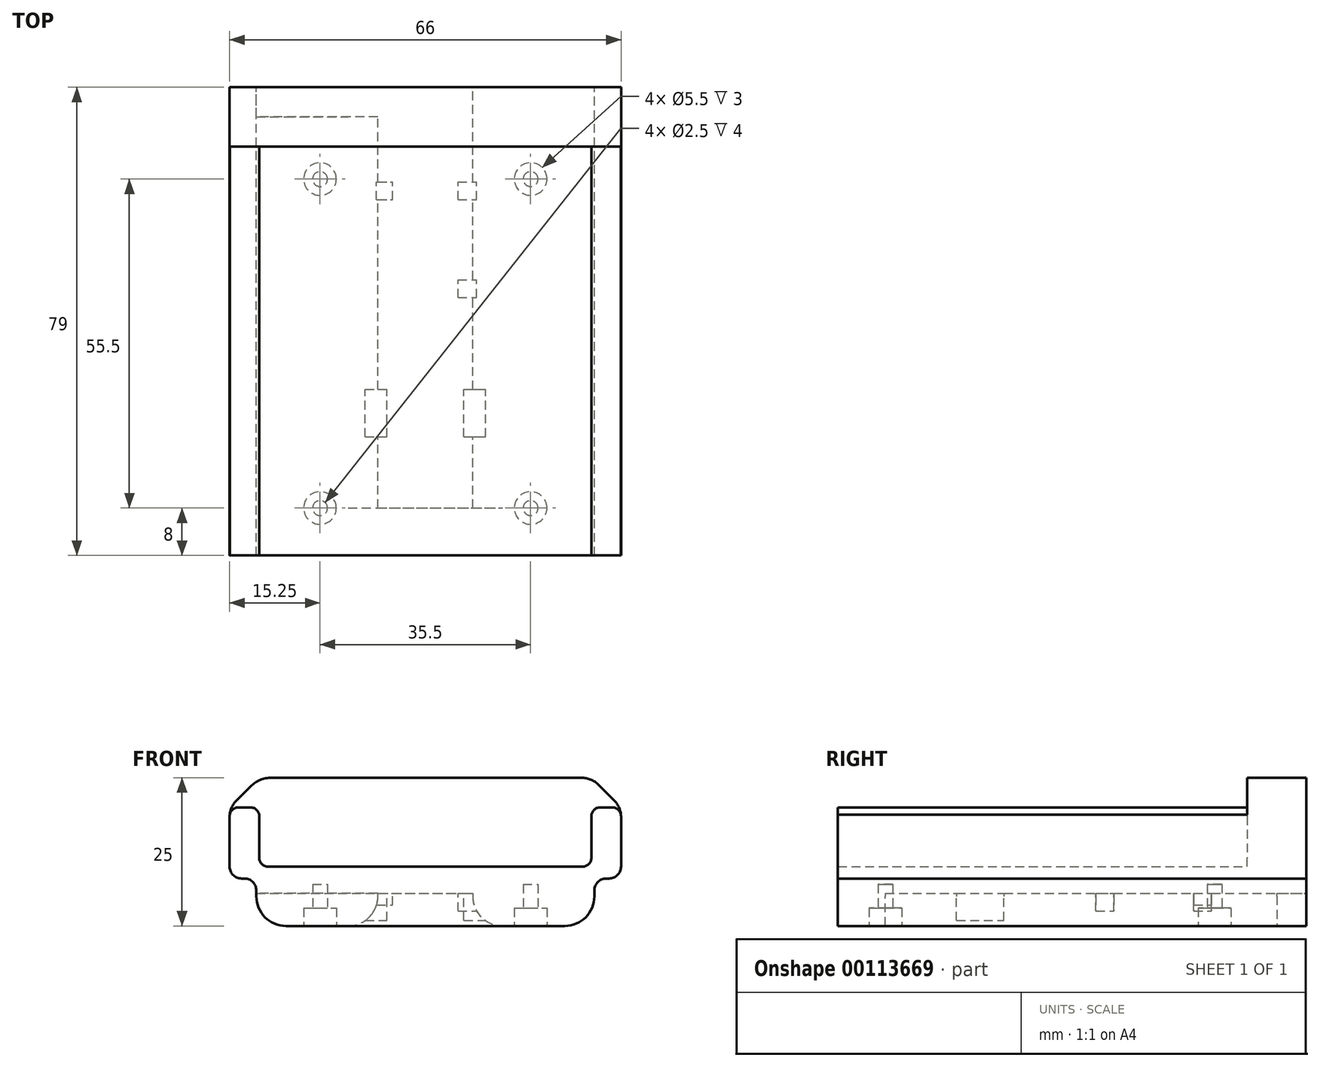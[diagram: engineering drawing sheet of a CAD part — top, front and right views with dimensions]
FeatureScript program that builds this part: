
annotation { "Feature Type Name" : "Feature", "Feature Type Description" : "" }
export const myFeature = defineFeature(function(context is Context, id is Id, definition is map)
    precondition{}
    {
        {
            var Q0;
            Q0=qCreatedBy(makeId("Front.planeOp"),FACE);
            var sketch = newSketch(context, id + "F0", { "sketchPlane" : qUnion([Q0])});
            skLineSegment(sketch, "E0.bottom", {"start": v(-33, 12.5) * mm, "end": v(33, 12.5) * mm});
            skLineSegment(sketch, "E0.top", {"start": v(-23.5, -12.5) * mm, "end": v(-13, -12.5) * mm});
            skLineSegment(sketch, "E0.left", {"start": v(-33, 12.5) * mm, "end": v(-33, -2.5) * mm});
            skLineSegment(sketch, "E0.right", {"start": v(33, 12.5) * mm, "end": v(33, -2.5) * mm});
            skLineSegment(sketch, "E1", {"start": v(28.5, -6.5) * mm, "end": v(28.5, -7.5) * mm});
            skLineSegment(sketch, "E2", {"start": v(-33, -4.5) * mm, "end": v(-33, -4.5) * mm});
            skLineSegment(sketch, "E3", {"start": v(-31, -4.5) * mm, "end": v(-30.5, -4.5) * mm});
            skLineSegment(sketch, "E4", {"start": v(-28.5, -6.5) * mm, "end": v(-28.5, -7.5) * mm});
            skArc(sketch, "E5.filletArc", {"start": v(-28.5, -6.5) * mm, "mid": v(-29.09, -5.09) * mm, "end": v(-30.5, -4.5) * mm});
            skLineSegment(sketch, "E6", {"start": v(30.5, -4.5) * mm, "end": v(31, -4.5) * mm});
            skPoint(sketch, "E7.visualSharp", {"position": v(28.5, -4.5) * mm});
            skArc(sketch, "E7.filletArc", {"start": v(30.5, -4.5) * mm, "mid": v(29.09, -5.09) * mm, "end": v(28.5, -6.5) * mm});
            skArc(sketch, "E8.filletArc", {"start": v(-33, -2.5) * mm, "mid": v(-32.41, -3.91) * mm, "end": v(-31, -4.5) * mm});
            skPoint(sketch, "E9.visualSharp", {"position": v(33, -4.5) * mm});
            skArc(sketch, "E9.filletArc", {"start": v(31, -4.5) * mm, "mid": v(32.41, -3.91) * mm, "end": v(33, -2.5) * mm});
            skLineSegment(sketch, "E10.bottom", {"start": v(-8, -7) * mm, "end": v(8, -7) * mm});
            skLineSegment(sketch, "E10.left", {"start": v(-8, -7) * mm, "end": v(-8, -7.5) * mm});
            skLineSegment(sketch, "E10.right", {"start": v(8, -7) * mm, "end": v(8, -7.5) * mm});
            skLineSegment(sketch, "E11.trimOffspring", {"start": v(13, -12.5) * mm, "end": v(23.5, -12.5) * mm});
            skPoint(sketch, "E12.visualSharp", {"position": v(-28.5, -12.5) * mm});
            skArc(sketch, "E12.filletArc", {"start": v(-28.5, -7.5) * mm, "mid": v(-27.04, -11.04) * mm, "end": v(-23.5, -12.5) * mm});
            skPoint(sketch, "E13.visualSharp", {"position": v(-8, -12.5) * mm});
            skArc(sketch, "E13.filletArc", {"start": v(-13, -12.5) * mm, "mid": v(-9.46, -11.04) * mm, "end": v(-8, -7.5) * mm});
            skPoint(sketch, "E14.visualSharp", {"position": v(8, -12.5) * mm});
            skArc(sketch, "E14.filletArc", {"start": v(8, -7.5) * mm, "mid": v(9.46, -11.04) * mm, "end": v(13, -12.5) * mm});
            skPoint(sketch, "E15.visualSharp", {"position": v(28.5, -12.5) * mm});
            skArc(sketch, "E15.filletArc", {"start": v(23.5, -12.5) * mm, "mid": v(27.04, -11.04) * mm, "end": v(28.5, -7.5) * mm});
            skSolve(sketch);
        }
        {
            var Q0;
            Q0 = qSketchRegion(id + "F0", true);
            extrude(context, id + "F1", {"entities" : qUnion([Q0]), "depth" : 71 * mm});
        }
        {
            var Q0;
            Q0=makeQuery(id+"F1.opExtrude","CAP_FACE",FACE,{"disambiguationData":[OSD([sQuery(id+"F0.wireOp",EDGE,"E0.bottom"),sQuery(id+"F0.wireOp",EDGE,"E0.top"),sQuery(id+"F0.wireOp",EDGE,"E0.left"),sQuery(id+"F0.wireOp",EDGE,"E0.right"),sQuery(id+"F0.wireOp",EDGE,"E1"),sQuery(id+"F0.wireOp",EDGE,"E3"),sQuery(id+"F0.wireOp",EDGE,"E4"),sQuery(id+"F0.wireOp",EDGE,"E5.filletArc"),sQuery(id+"F0.wireOp",EDGE,"E6"),sQuery(id+"F0.wireOp",EDGE,"E7.filletArc"),sQuery(id+"F0.wireOp",EDGE,"E8.filletArc"),sQuery(id+"F0.wireOp",EDGE,"E9.filletArc"),sQuery(id+"F0.wireOp",EDGE,"E10.bottom"),sQuery(id+"F0.wireOp",EDGE,"E10.left"),sQuery(id+"F0.wireOp",EDGE,"E10.right"),sQuery(id+"F0.wireOp",EDGE,"E11.trimOffspring"),sQuery(id+"F0.wireOp",EDGE,"E12.filletArc"),sQuery(id+"F0.wireOp",EDGE,"E13.filletArc"),sQuery(id+"F0.wireOp",EDGE,"E14.filletArc"),sQuery(id+"F0.wireOp",EDGE,"E15.filletArc")])],"isStart":false});
            var sketch = newSketch(context, id + "F2", { "sketchPlane" : qUnion([Q0])});
            skLineSegment(sketch, "E16", {"start": v(33, 6) * mm, "end": v(33, -2.32) * mm});
            skLineSegment(sketch, "E17", {"start": v(-23.5, -12.5) * mm, "end": v(23.5, -12.5) * mm});
            skLineSegment(sketch, "E18", {"start": v(-28.5, -6.5) * mm, "end": v(-28.5, -7.5) * mm});
            skLineSegment(sketch, "E19", {"start": v(28.5, -6.5) * mm, "end": v(28.5, -7.5) * mm});
            skPoint(sketch, "E20.trimOffspring.start.orphan", {"position": v(-33, -12.5) * mm});
            skPoint(sketch, "E21.orphan", {"position": v(-33, -7) * mm});
            skLineSegment(sketch, "E22", {"start": v(-33, 6) * mm, "end": v(-33, -2.5) * mm});
            skLineSegment(sketch, "E23", {"start": v(-33, -2.5) * mm, "end": v(-33, -2.5) * mm});
            skLineSegment(sketch, "E24", {"start": v(-31, -4.5) * mm, "end": v(-30.5, -4.5) * mm});
            skLineSegment(sketch, "E25", {"start": v(33, -2.32) * mm, "end": v(33, -2.5) * mm});
            skLineSegment(sketch, "E26", {"start": v(31, -4.5) * mm, "end": v(30.5, -4.5) * mm});
            skPoint(sketch, "E27.visualSharp", {"position": v(33, -4.5) * mm});
            skArc(sketch, "E27.filletArc", {"start": v(31, -4.5) * mm, "mid": v(32.41, -3.91) * mm, "end": v(33, -2.5) * mm});
            skPoint(sketch, "E28.newPointB", {"position": v(28.5, -2.32) * mm});
            skArc(sketch, "E28.filletArc", {"start": v(30.5, -4.5) * mm, "mid": v(29.09, -5.09) * mm, "end": v(28.5, -6.5) * mm});
            skPoint(sketch, "E29.visualSharp", {"position": v(-33, -4.5) * mm});
            skArc(sketch, "E29.filletArc", {"start": v(-33, -2.5) * mm, "mid": v(-32.41, -3.91) * mm, "end": v(-31, -4.5) * mm});
            skPoint(sketch, "E30.newPointB", {"position": v(-28.5, -2.49) * mm});
            skArc(sketch, "E30.filletArc", {"start": v(-28.5, -6.5) * mm, "mid": v(-29.09, -5.09) * mm, "end": v(-30.5, -4.5) * mm});
            skPoint(sketch, "E31.visualSharp", {"position": v(-28.5, -12.5) * mm});
            skArc(sketch, "E31.filletArc", {"start": v(-28.5, -7.5) * mm, "mid": v(-27.04, -11.04) * mm, "end": v(-23.5, -12.5) * mm});
            skPoint(sketch, "E32.visualSharp", {"position": v(28.5, -12.5) * mm});
            skArc(sketch, "E32.filletArc", {"start": v(23.5, -12.5) * mm, "mid": v(27.04, -11.04) * mm, "end": v(28.5, -7.5) * mm});
            skLineSegment(sketch, "E33", {"start": v(-31.5, 7.5) * mm, "end": v(-29.5, 7.5) * mm});
            skLineSegment(sketch, "E34", {"start": v(-28, 6) * mm, "end": v(-28, -1) * mm});
            skLineSegment(sketch, "E35", {"start": v(28, 6) * mm, "end": v(28, -1) * mm});
            skLineSegment(sketch, "E36", {"start": v(-26.5, -2.5) * mm, "end": v(26.5, -2.5) * mm});
            skLineSegment(sketch, "E37.trimOffspring", {"start": v(29.5, 7.5) * mm, "end": v(31.5, 7.5) * mm});
            skPoint(sketch, "E38.visualSharp", {"position": v(-33, 7.5) * mm});
            skArc(sketch, "E38.filletArc", {"start": v(-31.5, 7.5) * mm, "mid": v(-32.56, 7.06) * mm, "end": v(-33, 6) * mm});
            skPoint(sketch, "E39.visualSharp", {"position": v(-28, 7.5) * mm});
            skArc(sketch, "E39.filletArc", {"start": v(-28, 6) * mm, "mid": v(-28.44, 7.06) * mm, "end": v(-29.5, 7.5) * mm});
            skPoint(sketch, "E40.visualSharp", {"position": v(33, 7.5) * mm});
            skArc(sketch, "E40.filletArc", {"start": v(33, 6) * mm, "mid": v(32.56, 7.06) * mm, "end": v(31.5, 7.5) * mm});
            skPoint(sketch, "E41.visualSharp", {"position": v(28, 7.5) * mm});
            skArc(sketch, "E41.filletArc", {"start": v(29.5, 7.5) * mm, "mid": v(28.44, 7.06) * mm, "end": v(28, 6) * mm});
            skPoint(sketch, "E42.visualSharp", {"position": v(-28, -2.5) * mm});
            skArc(sketch, "E42.filletArc", {"start": v(-28, -1) * mm, "mid": v(-27.56, -2.06) * mm, "end": v(-26.5, -2.5) * mm});
            skPoint(sketch, "E43.visualSharp", {"position": v(28, -2.5) * mm});
            skArc(sketch, "E43.filletArc", {"start": v(26.5, -2.5) * mm, "mid": v(27.56, -2.06) * mm, "end": v(28, -1) * mm});
            skSolve(sketch);
        }
        {
            var Q0;
            Q0 = qSketchRegion(id + "F2", true);
            extrude(context, id + "F3", {"entities" : qUnion([Q0]), "operationType" : NewBodyOperationType.ADD, "depth" : 8 * mm});
        }
        {
            var Q0;
            Q0=makeQuery(id+"F1.opExtrude","CAP_FACE",FACE,{"disambiguationData":[OSD([sQuery(id+"F0.wireOp",EDGE,"E0.bottom"),sQuery(id+"F0.wireOp",EDGE,"E0.top"),sQuery(id+"F0.wireOp",EDGE,"E0.left"),sQuery(id+"F0.wireOp",EDGE,"E0.right"),sQuery(id+"F0.wireOp",EDGE,"E1"),sQuery(id+"F0.wireOp",EDGE,"E3"),sQuery(id+"F0.wireOp",EDGE,"E4"),sQuery(id+"F0.wireOp",EDGE,"E5.filletArc"),sQuery(id+"F0.wireOp",EDGE,"E6"),sQuery(id+"F0.wireOp",EDGE,"E7.filletArc"),sQuery(id+"F0.wireOp",EDGE,"E8.filletArc"),sQuery(id+"F0.wireOp",EDGE,"E9.filletArc"),sQuery(id+"F0.wireOp",EDGE,"E10.bottom"),sQuery(id+"F0.wireOp",EDGE,"E10.left"),sQuery(id+"F0.wireOp",EDGE,"E10.right"),sQuery(id+"F0.wireOp",EDGE,"E11.trimOffspring"),sQuery(id+"F0.wireOp",EDGE,"E12.filletArc"),sQuery(id+"F0.wireOp",EDGE,"E13.filletArc"),sQuery(id+"F0.wireOp",EDGE,"E14.filletArc"),sQuery(id+"F0.wireOp",EDGE,"E15.filletArc")])],"isStart":false});
            var sketch = newSketch(context, id + "F4", { "sketchPlane" : qUnion([Q0])});
            skLineSegment(sketch, "E44", {"start": v(-33, 6) * mm, "end": v(-33, 6) * mm});
            skLineSegment(sketch, "E45", {"start": v(-28, 6) * mm, "end": v(-28, -1) * mm});
            skLineSegment(sketch, "E46", {"start": v(-26.5, -2.5) * mm, "end": v(26.5, -2.5) * mm});
            skLineSegment(sketch, "E47", {"start": v(28, -1) * mm, "end": v(28, 6) * mm});
            skLineSegment(sketch, "E48", {"start": v(29.5, 7.5) * mm, "end": v(31.5, 7.5) * mm});
            skLineSegment(sketch, "E49", {"start": v(33, 12.5) * mm, "end": v(-33, 12.5) * mm});
            skLineSegment(sketch, "E50", {"start": v(-31.5, 7.5) * mm, "end": v(-29.5, 7.5) * mm});
            skLineSegment(sketch, "E51", {"start": v(-28, 6) * mm, "end": v(-28, 6) * mm});
            skPoint(sketch, "E52.newPointA", {"position": v(-33, 7.5) * mm});
            skArc(sketch, "E52.filletArc", {"start": v(-31.5, 7.5) * mm, "mid": v(-32.56, 7.06) * mm, "end": v(-33, 6) * mm});
            skPoint(sketch, "E53.visualSharp", {"position": v(-28, 7.5) * mm});
            skArc(sketch, "E53.filletArc", {"start": v(-28, 6) * mm, "mid": v(-28.44, 7.06) * mm, "end": v(-29.5, 7.5) * mm});
            skLineSegment(sketch, "E54", {"start": v(-33, 12.5) * mm, "end": v(-33, 6) * mm});
            skPoint(sketch, "E55.visualSharp", {"position": v(-28, -2.5) * mm});
            skArc(sketch, "E55.filletArc", {"start": v(-28, -1) * mm, "mid": v(-27.56, -2.06) * mm, "end": v(-26.5, -2.5) * mm});
            skPoint(sketch, "E56.visualSharp", {"position": v(28, -2.5) * mm});
            skArc(sketch, "E56.filletArc", {"start": v(26.5, -2.5) * mm, "mid": v(27.56, -2.06) * mm, "end": v(28, -1) * mm});
            skPoint(sketch, "E57.visualSharp", {"position": v(28, 7.5) * mm});
            skArc(sketch, "E57.filletArc", {"start": v(29.5, 7.5) * mm, "mid": v(28.44, 7.06) * mm, "end": v(28, 6) * mm});
            skArc(sketch, "E58.filletArc", {"start": v(33, 6) * mm, "mid": v(32.56, 7.06) * mm, "end": v(31.5, 7.5) * mm});
            skLineSegment(sketch, "E59", {"start": v(33, 6) * mm, "end": v(33, 12.5) * mm});
            skSolve(sketch);
        }
        {
            var Q0;
            Q0 = qSketchRegion(id + "F4", true);
            extrude(context, id + "F5", {"entities" : qUnion([Q0]), "operationType" : NewBodyOperationType.REMOVE, "oppositeDirection" : true, "depth" : 61 * mm});
        }
        {
            var Q0;
            Q0=makeQuery(id+"F1.opExtrude","SWEPT_EDGE",EDGE,{"disambiguationData":[OSD([sQuery(id+"F0.wireOp",EDGE,"E0.bottom"),sQuery(id+"F0.wireOp",EDGE,"E0.left")])]});
            chamfer(context, id + "F6", {"entities" : qUnion([Q0]), "width" : 5 * mm, "tangentPropagation" : true});
        }
        {
            var Q0;
            Q0=makeQuery(id+"F1.opExtrude","SWEPT_EDGE",EDGE,{"disambiguationData":[OSD([sQuery(id+"F0.wireOp",EDGE,"E0.bottom"),sQuery(id+"F0.wireOp",EDGE,"E0.right")])]});
            chamfer(context, id + "F7", {"entities" : qUnion([Q0]), "width" : 5 * mm, "tangentPropagation" : true});
        }
        {
            var Q0;
            {var subQ0=sQuery(id+"F0.wireOp",EDGE,"E0.bottom");Q0=makeQuery(id+"F7.opChamfer","BLEND_EDGE",EDGE,{"blendedFrom":[makeQuery(id+"F1.opExtrude","SWEPT_EDGE",EDGE,{"disambiguationData":[OSD([subQ0,sQuery(id+"F0.wireOp",EDGE,"E0.right")])]}),makeQuery(id+"F1.opExtrude","SWEPT_FACE",FACE,{"disambiguationData":[OSD([subQ0])]})],"blendedInto":[makeQuery(id+"F1.opExtrude","SWEPT_FACE",FACE,{"disambiguationData":[OSD([subQ0])]})]});}
            fillet(context, id + "F8", {"entities" : qUnion([Q0]), "radius" : 4 * mm, "tangentPropagation" : true, "allowEdgeOverflow" : false});
        }
        {
            var Q0;
            {var subQ0=sQuery(id+"F0.wireOp",EDGE,"E0.right");Q0=makeQuery(id+"F7.opChamfer","BLEND_EDGE",EDGE,{"blendedFrom":[makeQuery(id+"F1.opExtrude","SWEPT_EDGE",EDGE,{"disambiguationData":[OSD([sQuery(id+"F0.wireOp",EDGE,"E0.bottom"),subQ0])]}),makeQuery(id+"F3.boolean.opBoolean","MERGE",FACE,{"derivedFrom":[makeQuery(id+"F1.opExtrude","SWEPT_FACE",FACE,{"disambiguationData":[OSD([subQ0])]}),makeQuery(id+"F3.opExtrude","SWEPT_FACE",FACE,{"disambiguationData":[OSD([sQuery(id+"F2.wireOp",EDGE,"E16"),sQuery(id+"F2.wireOp",EDGE,"E25")])]})]})],"blendedInto":[makeQuery(id+"F3.boolean.opBoolean","MERGE",FACE,{"derivedFrom":[makeQuery(id+"F1.opExtrude","SWEPT_FACE",FACE,{"disambiguationData":[OSD([subQ0])]}),makeQuery(id+"F3.opExtrude","SWEPT_FACE",FACE,{"disambiguationData":[OSD([sQuery(id+"F2.wireOp",EDGE,"E16"),sQuery(id+"F2.wireOp",EDGE,"E25")])]})]})]});}
            fillet(context, id + "F9", {"entities" : qUnion([Q0]), "radius" : 4 * mm, "tangentPropagation" : true, "allowEdgeOverflow" : false});
        }
        {
            var Q0;
            {var subQ0=sQuery(id+"F0.wireOp",EDGE,"E0.left");Q0=makeQuery(id+"F6.opChamfer","BLEND_EDGE",EDGE,{"blendedFrom":[makeQuery(id+"F1.opExtrude","SWEPT_EDGE",EDGE,{"disambiguationData":[OSD([sQuery(id+"F0.wireOp",EDGE,"E0.bottom"),subQ0])]}),makeQuery(id+"F3.boolean.opBoolean","MERGE",FACE,{"derivedFrom":[makeQuery(id+"F1.opExtrude","SWEPT_FACE",FACE,{"disambiguationData":[OSD([subQ0])]}),makeQuery(id+"F3.opExtrude","SWEPT_FACE",FACE,{"disambiguationData":[OSD([sQuery(id+"F2.wireOp",EDGE,"E22")])]})]})],"blendedInto":[makeQuery(id+"F3.boolean.opBoolean","MERGE",FACE,{"derivedFrom":[makeQuery(id+"F1.opExtrude","SWEPT_FACE",FACE,{"disambiguationData":[OSD([subQ0])]}),makeQuery(id+"F3.opExtrude","SWEPT_FACE",FACE,{"disambiguationData":[OSD([sQuery(id+"F2.wireOp",EDGE,"E22")])]})]})]});}
            fillet(context, id + "F10", {"entities" : qUnion([Q0]), "radius" : 4 * mm, "tangentPropagation" : true, "allowEdgeOverflow" : false});
        }
        {
            var Q0;
            {var subQ0=sQuery(id+"F0.wireOp",EDGE,"E0.bottom");Q0=makeQuery(id+"F6.opChamfer","BLEND_EDGE",EDGE,{"blendedFrom":[makeQuery(id+"F1.opExtrude","SWEPT_EDGE",EDGE,{"disambiguationData":[OSD([subQ0,sQuery(id+"F0.wireOp",EDGE,"E0.left")])]}),makeQuery(id+"F1.opExtrude","SWEPT_FACE",FACE,{"disambiguationData":[OSD([subQ0])]})],"blendedInto":[makeQuery(id+"F1.opExtrude","SWEPT_FACE",FACE,{"disambiguationData":[OSD([subQ0])]})]});}
            fillet(context, id + "F11", {"entities" : qUnion([Q0]), "radius" : 5 * mm, "tangentPropagation" : true, "allowEdgeOverflow" : false});
        }
        {
            var Q0;
            Q0=makeQuery(id+"F1.opExtrude","SWEPT_FACE",FACE,{"disambiguationData":[OSD([sQuery(id+"F0.wireOp",EDGE,"E10.bottom")])]});
            var sketch = newSketch(context, id + "F12", { "sketchPlane" : qUnion([Q0])});
            skLineSegment(sketch, "E60.bottom", {"start": v(-11.5, 59) * mm, "end": v(-6.5, 59) * mm});
            skLineSegment(sketch, "E60.top", {"start": v(-11.5, 51) * mm, "end": v(-6.5, 51) * mm});
            skLineSegment(sketch, "E60.left", {"start": v(-11.5, 59) * mm, "end": v(-11.5, 51) * mm});
            skLineSegment(sketch, "E60.right", {"start": v(-6.5, 59) * mm, "end": v(-6.5, 51) * mm});
            skLineSegment(sketch, "E61.bottom", {"start": v(6.5, 59) * mm, "end": v(11.5, 59) * mm});
            skLineSegment(sketch, "E61.top", {"start": v(6.5, 51) * mm, "end": v(11.5, 51) * mm});
            skLineSegment(sketch, "E61.left", {"start": v(6.5, 59) * mm, "end": v(6.5, 51) * mm});
            skLineSegment(sketch, "E61.right", {"start": v(11.5, 59) * mm, "end": v(11.5, 51) * mm});
            skSolve(sketch);
        }
        {
            var Q0;
            Q0 = qSketchRegion(id + "F12", true);
            extrude(context, id + "F13", {"entities" : qUnion([Q0]), "operationType" : NewBodyOperationType.ADD, "depth" : 4.6 * mm});
        }
        {
            var Q0;
            Q0=makeQuery(id+"F1.opExtrude","SWEPT_FACE",FACE,{"disambiguationData":[OSD([sQuery(id+"F0.wireOp",EDGE,"E10.bottom")])]});
            var sketch = newSketch(context, id + "F14", { "sketchPlane" : qUnion([Q0])});
            skLineSegment(sketch, "E62.bottom", {"start": v(5.5, 35.5) * mm, "end": v(10.5, 35.5) * mm});
            skLineSegment(sketch, "E62.top", {"start": v(5.5, 32.5) * mm, "end": v(10.5, 32.5) * mm});
            skLineSegment(sketch, "E62.left", {"start": v(5.5, 35.5) * mm, "end": v(5.5, 32.5) * mm});
            skLineSegment(sketch, "E62.right", {"start": v(10.5, 35.5) * mm, "end": v(10.5, 32.5) * mm});
            skLineSegment(sketch, "E63.bottom", {"start": v(5.5, 19) * mm, "end": v(10.5, 19) * mm});
            skLineSegment(sketch, "E63.top", {"start": v(5.5, 16) * mm, "end": v(10.5, 16) * mm});
            skLineSegment(sketch, "E63.left", {"start": v(5.5, 19) * mm, "end": v(5.5, 16) * mm});
            skLineSegment(sketch, "E63.right", {"start": v(10.5, 19) * mm, "end": v(10.5, 16) * mm});
            skSolve(sketch);
        }
        {
            var Q0;
            Q0 = qSketchRegion(id + "F14", true);
            extrude(context, id + "F15", {"entities" : qUnion([Q0]), "operationType" : NewBodyOperationType.ADD, "depth" : 3 * mm});
        }
        {
            var Q0;
            Q0=makeQuery(id+"F1.opExtrude","SWEPT_FACE",FACE,{"disambiguationData":[OSD([sQuery(id+"F0.wireOp",EDGE,"E10.bottom")])]});
            var sketch = newSketch(context, id + "F16", { "sketchPlane" : qUnion([Q0])});
            skLineSegment(sketch, "E64.bottom", {"start": v(-10.5, 19) * mm, "end": v(-5.5, 19) * mm});
            skLineSegment(sketch, "E64.top", {"start": v(-10.5, 16) * mm, "end": v(-5.5, 16) * mm});
            skLineSegment(sketch, "E64.left", {"start": v(-10.5, 19) * mm, "end": v(-10.5, 16) * mm});
            skLineSegment(sketch, "E64.right", {"start": v(-5.5, 19) * mm, "end": v(-5.5, 16) * mm});
            skSolve(sketch);
        }
        {
            var Q0;
            Q0 = qSketchRegion(id + "F16", true);
            extrude(context, id + "F17", {"entities" : qUnion([Q0]), "operationType" : NewBodyOperationType.ADD, "depth" : 2 * mm});
        }
        {
            var Q0;
            Q0=makeQuery(id+"F1.opExtrude","CAP_FACE",FACE,{"disambiguationData":[OSD([sQuery(id+"F0.wireOp",EDGE,"E0.bottom"),sQuery(id+"F0.wireOp",EDGE,"E0.top"),sQuery(id+"F0.wireOp",EDGE,"E0.left"),sQuery(id+"F0.wireOp",EDGE,"E0.right"),sQuery(id+"F0.wireOp",EDGE,"E1"),sQuery(id+"F0.wireOp",EDGE,"E3"),sQuery(id+"F0.wireOp",EDGE,"E4"),sQuery(id+"F0.wireOp",EDGE,"E5.filletArc"),sQuery(id+"F0.wireOp",EDGE,"E6"),sQuery(id+"F0.wireOp",EDGE,"E7.filletArc"),sQuery(id+"F0.wireOp",EDGE,"E8.filletArc"),sQuery(id+"F0.wireOp",EDGE,"E9.filletArc"),sQuery(id+"F0.wireOp",EDGE,"E10.bottom"),sQuery(id+"F0.wireOp",EDGE,"E10.left"),sQuery(id+"F0.wireOp",EDGE,"E10.right"),sQuery(id+"F0.wireOp",EDGE,"E11.trimOffspring"),sQuery(id+"F0.wireOp",EDGE,"E12.filletArc"),sQuery(id+"F0.wireOp",EDGE,"E13.filletArc"),sQuery(id+"F0.wireOp",EDGE,"E14.filletArc"),sQuery(id+"F0.wireOp",EDGE,"E15.filletArc")])],"isStart":true});
            var sketch = newSketch(context, id + "F18", { "sketchPlane" : qUnion([Q0])});
            skLineSegment(sketch, "E65", {"start": v(-1.5, -7) * mm, "end": v(28.5, -7) * mm});
            skLineSegment(sketch, "E66", {"start": v(28.5, -7) * mm, "end": v(28.5, -7.5) * mm});
            skLineSegment(sketch, "E67", {"start": v(23.5, -12.5) * mm, "end": v(13, -12.5) * mm});
            skLineSegment(sketch, "E68", {"start": v(8, -7) * mm, "end": v(8, -7.5) * mm});
            skPoint(sketch, "E69.newPointB", {"position": v(-8, -12.5) * mm});
            skArc(sketch, "E69.filletArc", {"start": v(8, -7.5) * mm, "mid": v(9.46, -11.04) * mm, "end": v(13, -12.5) * mm});
            skPoint(sketch, "E70.visualSharp", {"position": v(28.5, -12.5) * mm});
            skArc(sketch, "E70.filletArc", {"start": v(23.5, -12.5) * mm, "mid": v(27.04, -11.04) * mm, "end": v(28.5, -7.5) * mm});
            skLineSegment(sketch, "E71", {"start": v(-1.5, -12.5) * mm, "end": v(13, -12.5) * mm});
            skLineSegment(sketch, "E72", {"start": v(-1.5, -7) * mm, "end": v(-1.5, -12.5) * mm});
            skPoint(sketch, "E73.end.orphan", {"position": v(-8, -7) * mm});
            skSolve(sketch);
        }
        {
            var Q0;
            Q0 = qSketchRegion(id + "F18", true);
            extrude(context, id + "F19", {"entities" : qUnion([Q0]), "operationType" : NewBodyOperationType.REMOVE, "oppositeDirection" : true, "depth" : 5 * mm});
        }
        {
            var Q0;
            Q0=makeQuery(id+"F3.boolean.opBoolean","MERGE",FACE,{"derivedFrom":[makeQuery(id+"F1.opExtrude","SWEPT_FACE",FACE,{"disambiguationData":[OSD([sQuery(id+"F0.wireOp",EDGE,"E0.top")])]}),makeQuery(id+"F1.opExtrude","SWEPT_FACE",FACE,{"disambiguationData":[OSD([sQuery(id+"F0.wireOp",EDGE,"E11.trimOffspring")])]}),makeQuery(id+"F3.opExtrude","SWEPT_FACE",FACE,{"disambiguationData":[OSD([sQuery(id+"F2.wireOp",EDGE,"E17")])]})]});
            var sketch = newSketch(context, id + "F20", { "sketchPlane" : qUnion([Q0])});
            skCircle(sketch, "E74", {"center": v(-17.75, 71) * mm, "radius": 2.75 * mm});
            skCircle(sketch, "E75", {"center": v(17.75, 71) * mm, "radius": 2.75 * mm});
            skCircle(sketch, "E76", {"center": v(17.75, 15.5) * mm, "radius": 2.75 * mm});
            skCircle(sketch, "E77", {"center": v(-17.75, 15.5) * mm, "radius": 2.75 * mm});
            skSolve(sketch);
        }
        {
            var Q0;
            Q0 = qSketchRegion(id + "F20", true);
            extrude(context, id + "F21", {"entities" : qUnion([Q0]), "operationType" : NewBodyOperationType.REMOVE, "oppositeDirection" : true, "depth" : 3 * mm});
        }
        {
            var Q0;
            Q0=makeQuery(id+"F3.boolean.opBoolean","MERGE",FACE,{"derivedFrom":[makeQuery(id+"F1.opExtrude","SWEPT_FACE",FACE,{"disambiguationData":[OSD([sQuery(id+"F0.wireOp",EDGE,"E0.top")])]}),makeQuery(id+"F1.opExtrude","SWEPT_FACE",FACE,{"disambiguationData":[OSD([sQuery(id+"F0.wireOp",EDGE,"E11.trimOffspring")])]}),makeQuery(id+"F3.opExtrude","SWEPT_FACE",FACE,{"disambiguationData":[OSD([sQuery(id+"F2.wireOp",EDGE,"E17")])]})]});
            var sketch = newSketch(context, id + "F22", { "sketchPlane" : qUnion([Q0])});
            skCircle(sketch, "E78", {"center": v(-17.75, 71) * mm, "radius": 1.25 * mm});
            skCircle(sketch, "E79", {"center": v(17.75, 71) * mm, "radius": 1.25 * mm});
            skCircle(sketch, "E80", {"center": v(-17.75, 15.5) * mm, "radius": 1.25 * mm});
            skCircle(sketch, "E81", {"center": v(17.75, 15.5) * mm, "radius": 1.25 * mm});
            skSolve(sketch);
        }
        {
            var Q0;
            Q0 = qSketchRegion(id + "F22", true);
            extrude(context, id + "F23", {"entities" : qUnion([Q0]), "operationType" : NewBodyOperationType.REMOVE, "oppositeDirection" : true, "depth" : 7 * mm});
        }
    });
